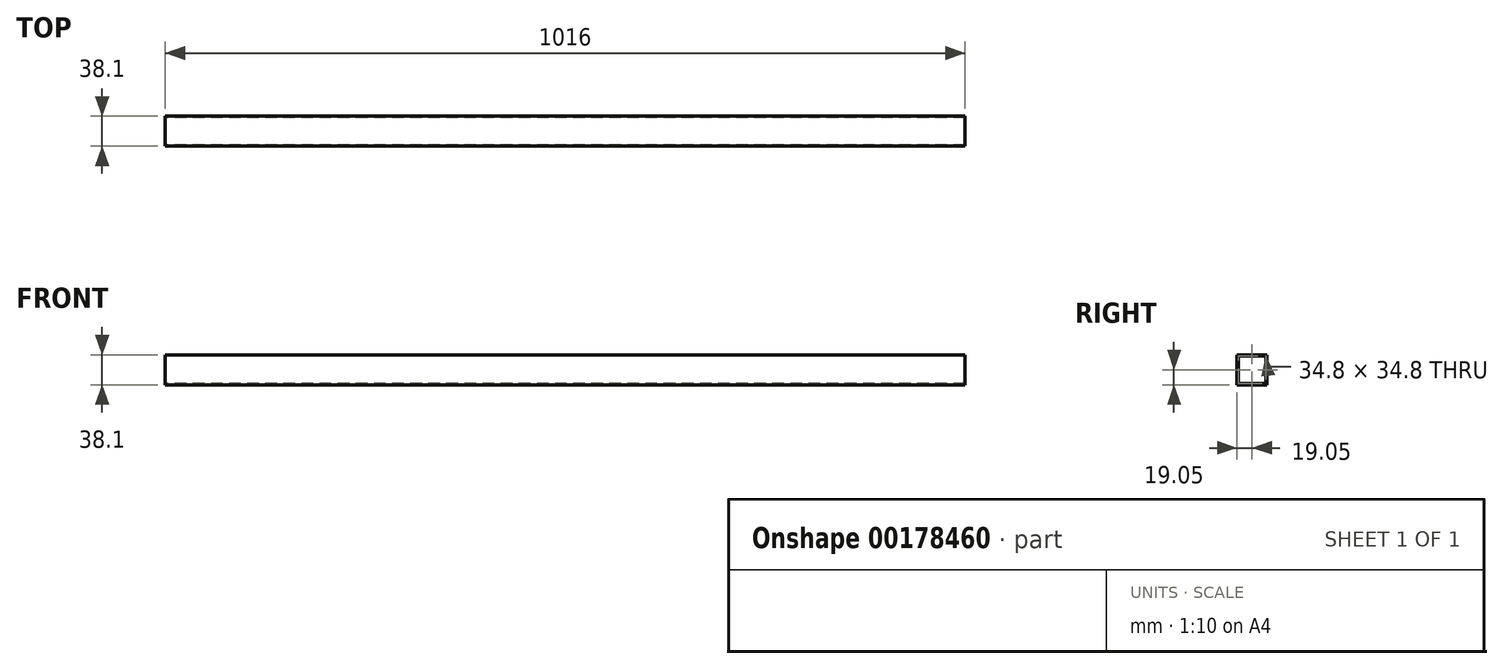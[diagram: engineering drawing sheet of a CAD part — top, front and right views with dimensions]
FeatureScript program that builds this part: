
annotation { "Feature Type Name" : "Feature", "Feature Type Description" : "" }
export const myFeature = defineFeature(function(context is Context, id is Id, definition is map)
    precondition{}
    {
        {
            var Q0;
            Q0=qCreatedBy(makeId("Right.planeOp"),FACE);
            var sketch = newSketch(context, id + "F0", { "sketchPlane" : qUnion([Q0])});
            skLineSegment(sketch, "E0.bottom", {"start": v(19.05, 19.05) * mm, "end": v(-19.05, 19.05) * mm});
            skLineSegment(sketch, "E0.top", {"start": v(19.05, -19.05) * mm, "end": v(-19.05, -19.05) * mm});
            skLineSegment(sketch, "E0.left", {"start": v(19.05, 19.05) * mm, "end": v(19.05, -19.05) * mm});
            skLineSegment(sketch, "E0.right", {"start": v(-19.05, 19.05) * mm, "end": v(-19.05, -19.05) * mm});
            skPoint(sketch, "E0.middle", {"position": v(0, 0) * mm});
            skLineSegment(sketch, "E1.bottom", {"start": v(17.4, 17.4) * mm, "end": v(-17.4, 17.4) * mm});
            skLineSegment(sketch, "E1.top", {"start": v(17.4, -17.4) * mm, "end": v(-17.4, -17.4) * mm});
            skLineSegment(sketch, "E1.left", {"start": v(17.4, 17.4) * mm, "end": v(17.4, -17.4) * mm});
            skLineSegment(sketch, "E1.right", {"start": v(-17.4, 17.4) * mm, "end": v(-17.4, -17.4) * mm});
            skSolve(sketch);
        }
        {
            var Q0;
            Q0=makeQuery(id+"F0.imprint","IMPRINT",FACE,{"disambiguationData":[TD([[makeQuery(id+"F0.imprint","IMPRINT",EDGE,{"derivedFrom":sQuery(id+"F0.wireOp",EDGE,"E0.bottom")}),1.0]])]});
            extrude(context, id + "F1", {"entities" : qUnion([Q0]), "depth" : 508 * mm, "hasSecondDirection" : true, "secondDirectionOppositeDirection" : true, "secondDirectionDepth" : 508 * mm});
        }
    });
